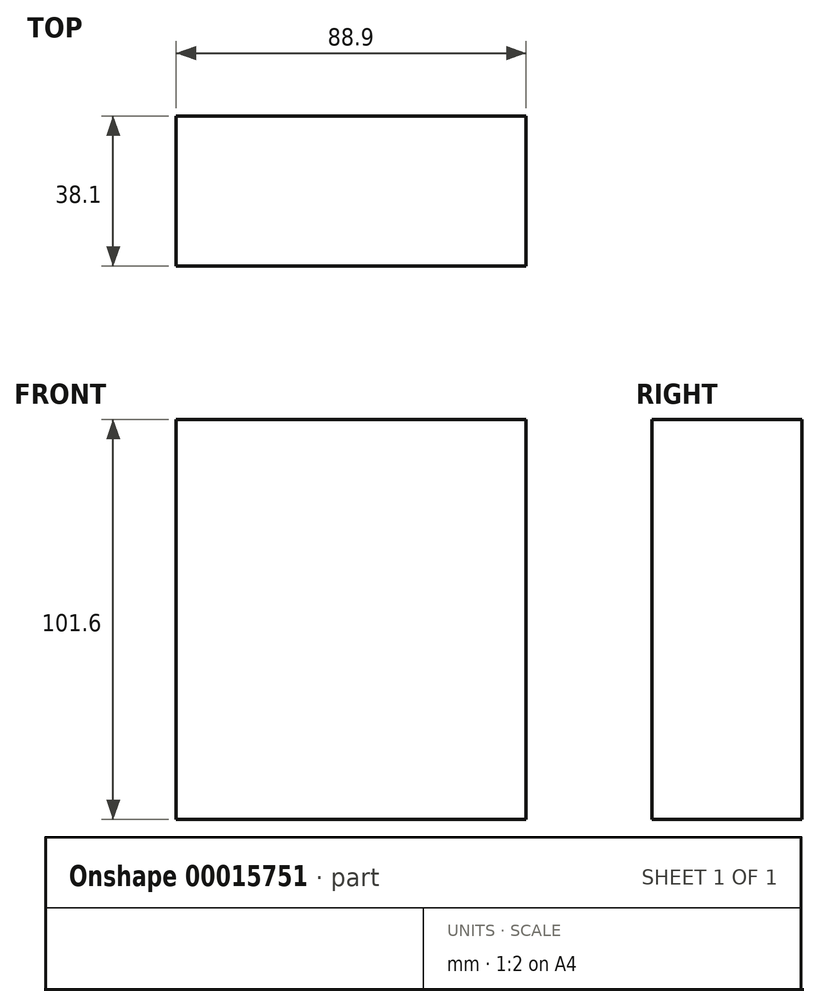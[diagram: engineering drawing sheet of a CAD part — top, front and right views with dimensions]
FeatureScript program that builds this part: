
annotation { "Feature Type Name" : "Feature", "Feature Type Description" : "" }
export const myFeature = defineFeature(function(context is Context, id is Id, definition is map)
    precondition{}
    {
        {
            var Q0;
            Q0=qCreatedBy(makeId("Top.planeOp"),FACE);
            var sketch = newSketch(context, id + "F0", { "sketchPlane" : qUnion([Q0])});
            skLineSegment(sketch, "E0.bottom", {"start": v(0, 0) * mm, "end": v(88.9, 0) * mm});
            skLineSegment(sketch, "E0.top", {"start": v(0, -38.1) * mm, "end": v(88.9, -38.1) * mm});
            skLineSegment(sketch, "E0.left", {"start": v(0, 0) * mm, "end": v(0, -38.1) * mm});
            skLineSegment(sketch, "E0.right", {"start": v(88.9, 0) * mm, "end": v(88.9, -38.1) * mm});
            skSolve(sketch);
        }
        {
            var Q0;
            Q0 = qSketchRegion(id + "F0", true);
            extrude(context, id + "F1", {"entities" : qUnion([Q0]), "depth" : 101.6 * mm});
        }
    });
